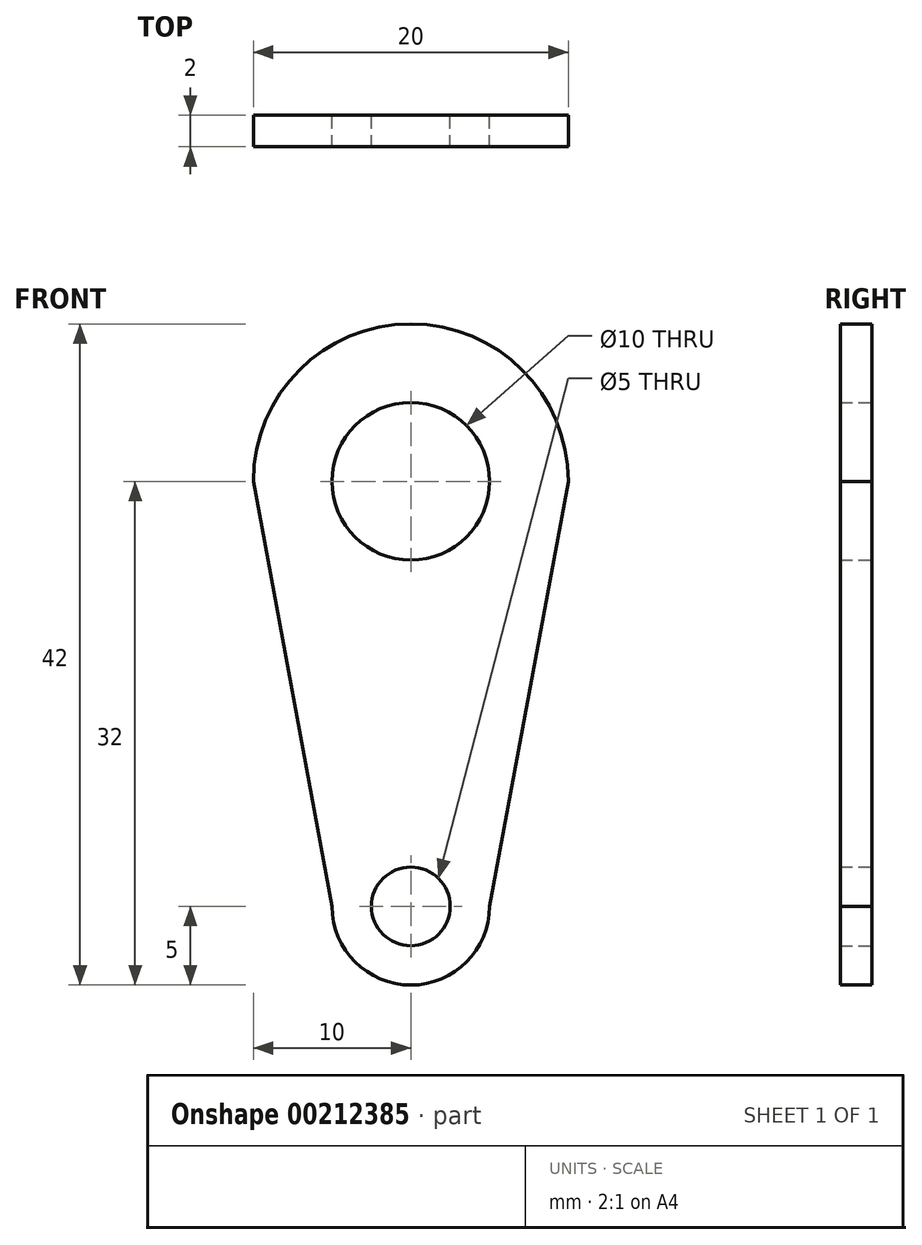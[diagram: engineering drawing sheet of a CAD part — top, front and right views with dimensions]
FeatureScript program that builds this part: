
annotation { "Feature Type Name" : "Feature", "Feature Type Description" : "" }
export const myFeature = defineFeature(function(context is Context, id is Id, definition is map)
    precondition{}
    {
        {
            var Q0;
            Q0=qCreatedBy(makeId("Front.planeOp"),FACE);
            var sketch = newSketch(context, id + "F0", { "sketchPlane" : qUnion([Q0])});
            skPoint(sketch, "E0.middle", {"position": v(0, 0) * mm});
            skCircle(sketch, "E1", {"center": v(0, 11) * mm, "radius": 5 * mm});
            skCircle(sketch, "E2", {"center": v(0, -16) * mm, "radius": 2.5 * mm});
            skPoint(sketch, "E2.centerSnap0", {"position": v(0, 21) * mm});
            skArc(sketch, "E3", {"start": v(-5, -16) * mm, "mid": v(0, -21) * mm, "end": v(5, -16) * mm});
            skLineSegment(sketch, "E4", {"start": v(-10, 11) * mm, "end": v(-5, -16) * mm});
            skLineSegment(sketch, "E5", {"start": v(10, 11) * mm, "end": v(5, -16) * mm});
            skArc(sketch, "E6.trimOffspring", {"start": v(10, 11) * mm, "mid": v(0, 21) * mm, "end": v(-10, 11) * mm});
            skSolve(sketch);
        }
        {
            var Q0;
            Q0=makeQuery(id+"F0.imprint","IMPRINT",FACE,{"disambiguationData":[TD([[makeQuery(id+"F0.imprint","IMPRINT",EDGE,{"derivedFrom":sQuery(id+"F0.wireOp",EDGE,"E1")}),-1.0]])]});
            extrude(context, id + "F1", {"entities" : qUnion([Q0]), "depth" : 2 * mm});
        }
    });
